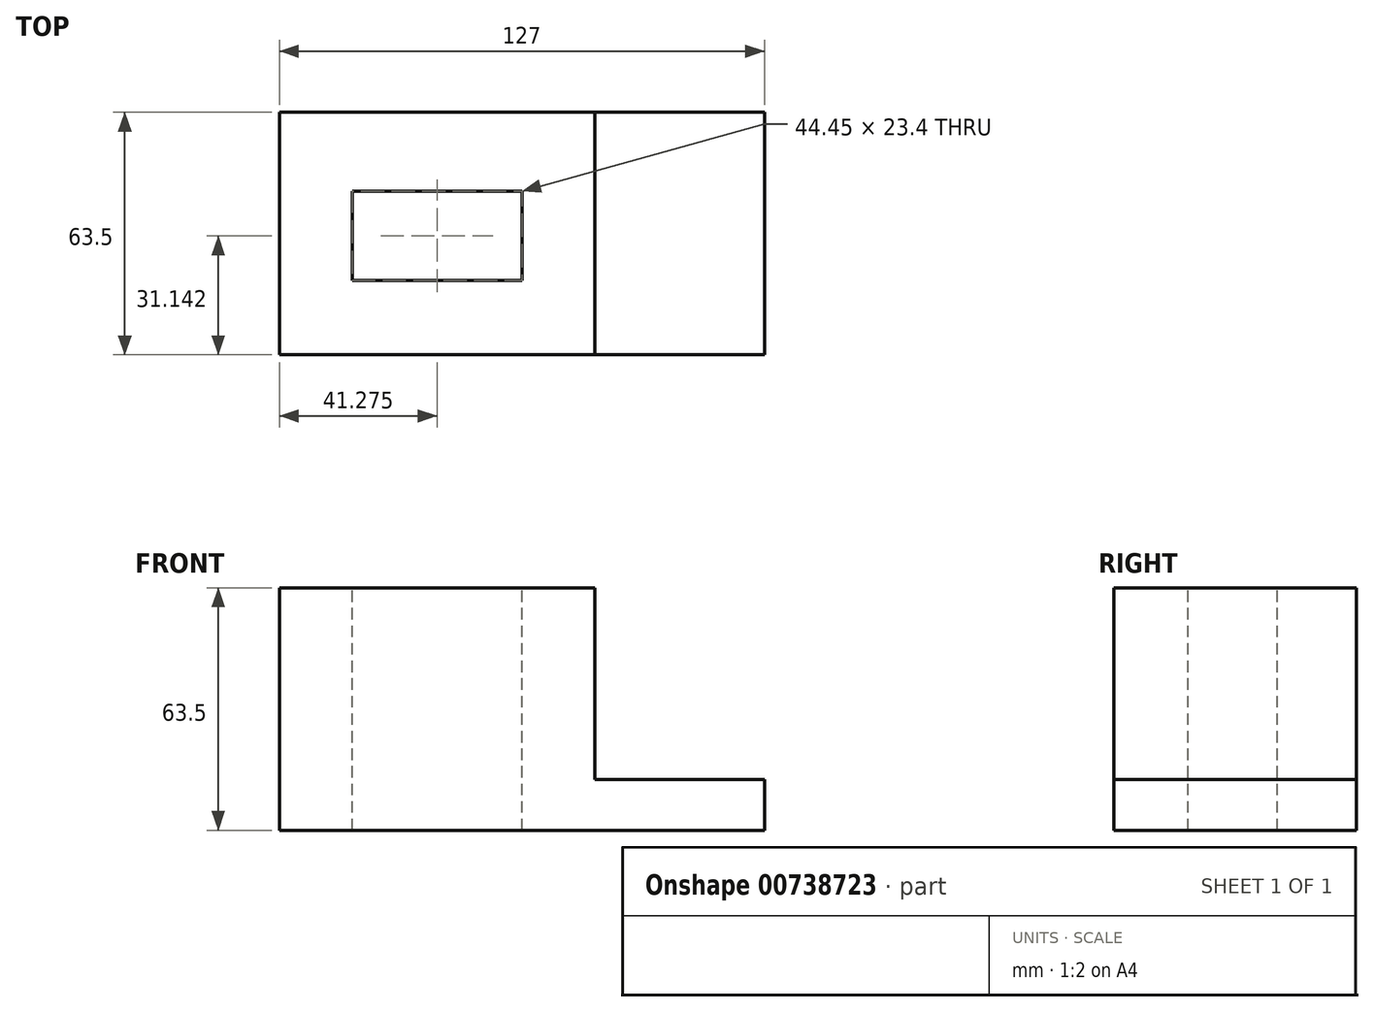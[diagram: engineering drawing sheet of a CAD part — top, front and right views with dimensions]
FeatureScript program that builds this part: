
annotation { "Feature Type Name" : "Feature", "Feature Type Description" : "" }
export const myFeature = defineFeature(function(context is Context, id is Id, definition is map)
    precondition{}
    {
        {
            var Q0;
            Q0=qCreatedBy(makeId("Top.planeOp"),FACE);
            var sketch = newSketch(context, id + "F0", { "sketchPlane" : qUnion([Q0])});
            skLineSegment(sketch, "E0.bottom", {"start": v(0, 0) * mm, "end": v(82.55, 0) * mm});
            skLineSegment(sketch, "E0.top", {"start": v(0, 63.5) * mm, "end": v(82.55, 63.5) * mm});
            skLineSegment(sketch, "E0.left", {"start": v(0, 0) * mm, "end": v(0, 63.5) * mm});
            skLineSegment(sketch, "E0.right", {"start": v(82.55, 0) * mm, "end": v(82.55, 63.5) * mm});
            skLineSegment(sketch, "E1.bottom", {"start": v(19.05, 19.44) * mm, "end": v(63.5, 19.44) * mm});
            skLineSegment(sketch, "E1.top", {"start": v(19.05, 42.84) * mm, "end": v(63.5, 42.84) * mm});
            skLineSegment(sketch, "E1.left", {"start": v(19.05, 19.44) * mm, "end": v(19.05, 42.84) * mm});
            skLineSegment(sketch, "E1.right", {"start": v(63.5, 19.44) * mm, "end": v(63.5, 42.84) * mm});
            skSolve(sketch);
        }
        {
            var Q0;
            Q0=makeQuery(id+"F0.imprint","IMPRINT",FACE,{"disambiguationData":[TD([[makeQuery(id+"F0.imprint","IMPRINT",EDGE,{"derivedFrom":sQuery(id+"F0.wireOp",EDGE,"E0.bottom")}),1.0]])]});
            extrude(context, id + "F1", {"entities" : qUnion([Q0]), "oppositeDirection" : true, "depth" : 63.5 * mm, "offsetDistance" : 25.4 * mm});
        }
        {
            var Q0;
            Q0=makeQuery(id+"F1.opExtrude","SWEPT_FACE",FACE,{"disambiguationData":[OSD([sQuery(id+"F0.wireOp",EDGE,"E0.right")])]});
            var sketch = newSketch(context, id + "F2", { "sketchPlane" : qUnion([Q0])});
            skLineSegment(sketch, "E2", {"start": v(0, -50.15) * mm, "end": v(63.5, -50.15) * mm});
            skSolve(sketch);
        }
        {
            var Q0;
            Q0 = qSketchRegion(id + "F2", true);
            var Q1;
            {var subQ0=sQuery(id+"F2.wireOp",EDGE,"E2");Q1=makeQuery(id+"F2.imprint","IMPRINT",FACE,{"disambiguationData":[TD([[makeQuery(id+"F2.imprint","IMPRINT",EDGE,{"derivedFrom":subQ0}),-1.0]])]});}
            extrude(context, id + "F3", {"entities" : qUnion([Q0, Q1]), "operationType" : NewBodyOperationType.ADD, "depth" : 44.45 * mm, "offsetDistance" : 25.4 * mm});
        }
    });
